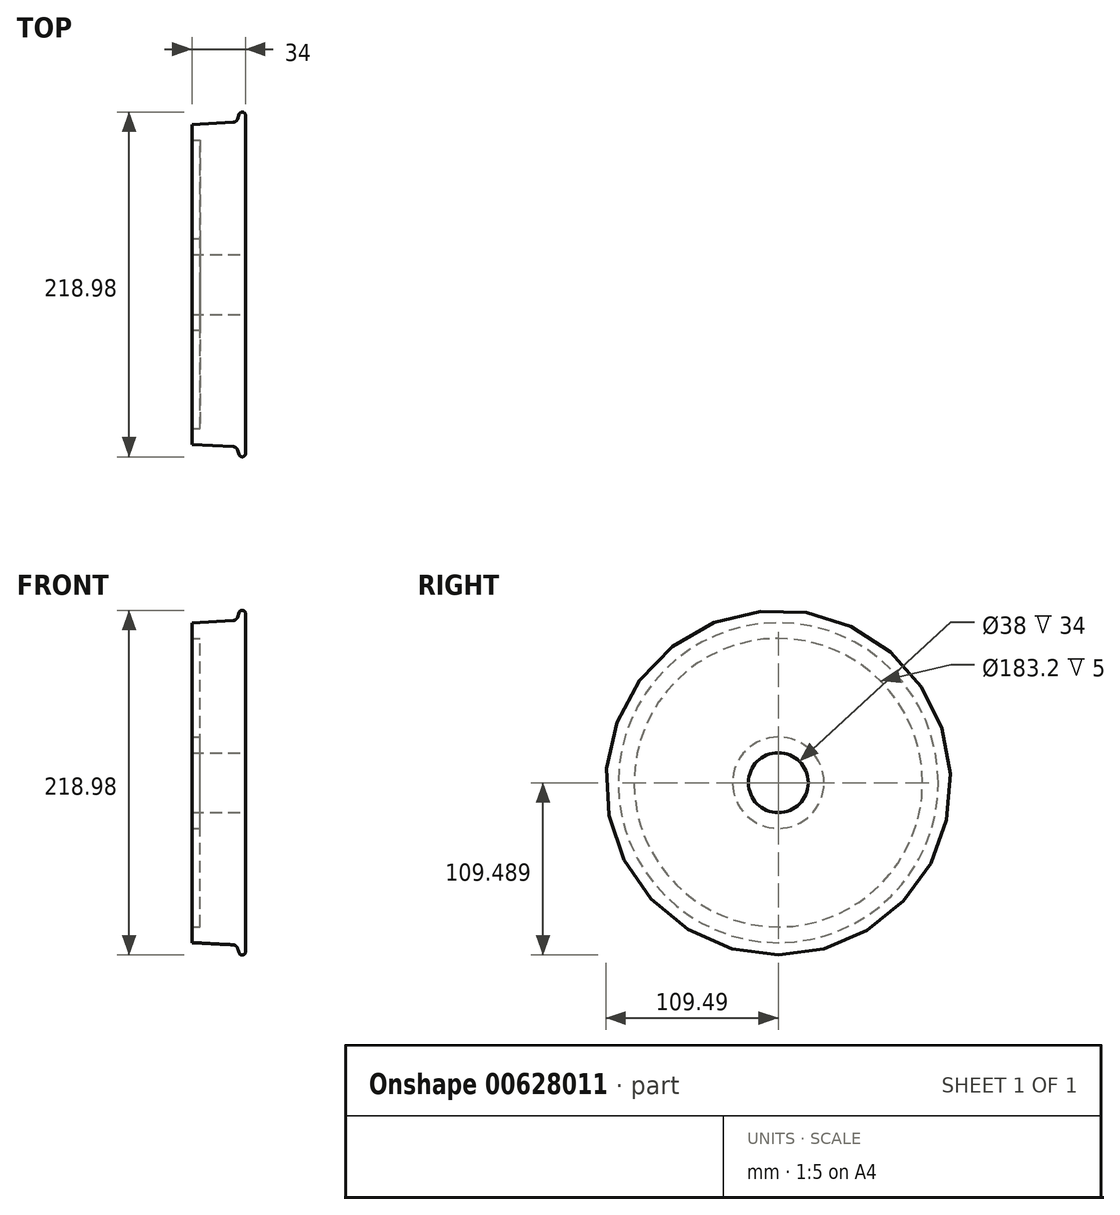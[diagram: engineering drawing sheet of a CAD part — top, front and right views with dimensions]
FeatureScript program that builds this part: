
annotation { "Feature Type Name" : "Feature", "Feature Type Description" : "" }
export const myFeature = defineFeature(function(context is Context, id is Id, definition is map)
    precondition{}
    {
        {
            var Q0;
            Q0=qCreatedBy(makeId("Front.planeOp"),FACE);
            var sketch = newSketch(context, id + "F0", { "sketchPlane" : qUnion([Q0])});
            skLineSegment(sketch, "E0.bottom", {"start": v(17, 49.68) * mm, "end": v(-17, 49.68) * mm, "construction": true});
            skLineSegment(sketch, "E0.top", {"start": v(17, -51.92) * mm, "end": v(-17, -51.92) * mm, "construction": true});
            skLineSegment(sketch, "E0.left", {"start": v(17, 49.68) * mm, "end": v(17, 30.68) * mm, "construction": true});
            skLineSegment(sketch, "E0.right", {"start": v(-17, 49.68) * mm, "end": v(-17, 30.68) * mm, "construction": true});
            skPoint(sketch, "E0.middle", {"position": v(0, -1.12) * mm});
            skLineSegment(sketch, "E1", {"start": v(-17, -51.92) * mm, "end": v(9.06, -53.29) * mm});
            skLineSegment(sketch, "E2", {"start": v(11.88, -55.37) * mm, "end": v(13, -58.46) * mm});
            skLineSegment(sketch, "E3", {"start": v(17, -51.92) * mm, "end": v(17, -57.75) * mm});
            skArc(sketch, "E4", {"start": v(17, -57.75) * mm, "mid": v(15.3, -59.78) * mm, "end": v(13, -58.46) * mm});
            skLineSegment(sketch, "E5", {"start": v(13, -58.46) * mm, "end": v(13, -51.92) * mm, "construction": true});
            skPoint(sketch, "E6.visualSharp", {"position": v(11.16, -53.4) * mm});
            skArc(sketch, "E6.filletArc", {"start": v(11.88, -55.37) * mm, "mid": v(10.79, -53.9) * mm, "end": v(9.06, -53.29) * mm});
            skLineSegment(sketch, "E7", {"start": v(-17, 30.68) * mm, "end": v(17, 30.68) * mm});
            skLineSegment(sketch, "E8", {"start": v(-17, 30.68) * mm, "end": v(-17, 20.68) * mm});
            skLineSegment(sketch, "E9", {"start": v(17, 30.68) * mm, "end": v(17, -51.92) * mm});
            skLineSegment(sketch, "E10", {"start": v(-17, -41.92) * mm, "end": v(-12, -41.92) * mm});
            skLineSegment(sketch, "E11", {"start": v(-12, -41.92) * mm, "end": v(-12, 20.68) * mm});
            skLineSegment(sketch, "E12", {"start": v(-12, 20.68) * mm, "end": v(-17, 20.68) * mm});
            skLineSegment(sketch, "E13", {"start": v(-17, -41.92) * mm, "end": v(-17, -51.92) * mm});
            skSolve(sketch);
        }
        {
            var Q0;
            Q0=makeQuery(id+"F0.imprint","IMPRINT",FACE,{"disambiguationData":[TD([[makeQuery(id+"F0.imprint","IMPRINT",EDGE,{"derivedFrom":sQuery(id+"F0.wireOp",EDGE,"E1")}),1.0]])]});
            var Q1;
            Q1=sQuery(id+"F0.wireOp",EDGE,"E0.bottom");
            revolve(context, id + "F1", {"entities" : qUnion([Q0]), "axis" : qUnion([Q1]), "revolveType" : RevolveType.FULL});
        }
    });
